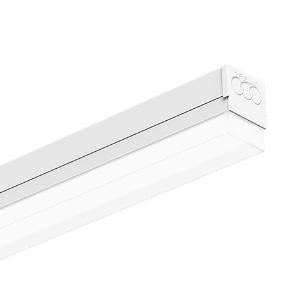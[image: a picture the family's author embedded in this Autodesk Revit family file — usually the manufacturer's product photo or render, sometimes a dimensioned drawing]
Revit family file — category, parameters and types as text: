
# Revit family: 3f_filippi_-_3f_zeta_dr_3f_filippi_-_10968_-_3f_zeta_dr_1x18_led_dali_l1194
name_source: partatom
category: Lighting Fixtures
units: mm (PartAtom-declared; Revit-internal decimal feet)

## family parameters
Cut with Voids When Loaded = No
Host = Face
Light Source = No
Part Type = Normal
Room Calculation Point = No
Round Connector Dimension = Use Diameter
Shared = No

## types (1)
- 3F Filippi - 3F Zeta DR (1 x LED, 2425 lm, 20 W, 4000 K)
    Apparent Load = 20 VA
    Approval mark = CE
    CIE Flux Codes = 41 72 91 86 100
    Color Rendering = 80
    Color Temperature = 4000 K
    Control Gear = Electronic transformer
    Default Elevation = 1800 mm
    Description = ILLUMINOTECHNICAL
Luminous efficiency 100% (DLOR 86%, ULOR 14%).
Initial luminous flux of the luminaire 2425 lm.
Diffused symmetric distribution.
Installation Interdistance Transv.D = 1.31 x hu - Long.D = 1.25 x hu.
Tabular UGR (CIE 117 - 4H-8H; S=0.25H; 70/50/20): RUG 23.1 - 21.7.
Beam angle: 136° - 112°.
Luminous efficacy 121 lm/W.
Lifetime (L93/B10): 30000 h. (tq+25°C)
Lifetime (L90/B10): 50000 h. (tq+25°C)
Lifetime (L85/B10): 80000 h. (tq+25°C)
Lifetime (L80/B10): 100000 h. (tq+25°C)
Sudden decreased luminous flux after 50000 hours: 0% (C0).
Photobiological safety in compliance with IEC/TR 62778: RG0 risk exempt, (IEC 62471).
In compliance with IEC/EN 62722-2-1 - IEC/EN 62717 standards.

SOURCE
Linear LED module 18W/840.
Energy efficiency class (UE 2019/2020 - UE 2019/2015): D.
CIE 13.3 Colour rendering index: CRI >80 (R9 <50%).
IES TM-30 Fidelity Index: Rf = 84 Rg = 95.
CCT nominal colour temperature 4000 K.
Colour initial tolerance (MacAdam): SDCM 3.

MECHANICAL
Housing in hot-galvanised steel, painted in white polyester, obtained through rolling process.
Light unit in hot-galvanised steel, painted in white polyester base with fixing springs and retractable safety hooks in stainless steel.
Rectangular screen in self-extinguishing polycarbonate, UV stabilised, opal, with smooth outer surface.
End caps in white polycarbonate.
Pair of stainless steel sliding brackets with sliding block screws.
Luminaire with limited surface temperature. - D - (EN 60598-2-24)
Dimensions: 1194x62 mm, height 81 mm. Weight 3.3 kg.
IP40 protection degree.
Mechanical strength to impacts IK06 (1 joule).
Glow-wire test resistance 850°C.

ELECTRICAL
Halogen Free DALI-2 DATI (Parts 251, 252, 253), PUSH-DIM, electronic wiring 230V-50/60Hz, power factor 0.90 at full load, THD <25%, constant output current, SELV, class I, 1 driver, 1 DALI addresse.
Power of the luminaire 20 W.
ENEC - CE.
SAFE FLICKER: PstLM=<1 and SVM=<0.4 (IEC TR 61547-1 and IEC TR 63158), to ensure a more comfortable and safe light.
Luminaire compliant with EN 60598-2-22 for power supply from a centralised emergency system CPSS (Central Power Supply System), not incorporated in the luminaire - high risk areas excluded. The default power and flux are 100% in AC and 15% in DC.
Ambient temperature from 0°C to +25°C.
Temperature class T6 max 85°C.
Relative humidity UR: <85%.

INSTALLATION
Ceiling / Suspended / Wall.
All accessories dedicated to this product are available on the Catalog and on our website www.3F-Filippi.com.

APPLICATIONS
Suitable product for food production plants (HACCP), IFS (Food Version 6), BRC (GSFS Food Version 7).
In commercial environments, exhibition areas, shops and stores.

LIGHT MANAGEMENT
Recommended minimum setting: 10%.
The luminaire, equipped with (DALI-2 DATI) driver, can be controlled manually with 3F Easy Dim technology or automatically/manually with wired or wireless DALI/D2D control systems.
The D2D driver guarantees interoperability with other devices with the same certification by making the following information available:
Device Data (Part 251), Energy Report (Part 252), Diagnosis & Maintenance (Part 253).
In electrical systems without a regulation system (manual or automatic) and DALI bus, a suitable jumper must be made on the DA-DA terminals of the appliance.

WARNING
Luminaire designed for disposal/recycling at end-of-life.
Replaceable (LED only) light source by a professional. Replaceable control gear by a professional.
    Height = 81 mm
    Lamp = 1 x LED
    Lamp Light Flux = 2425 lm
    Lamp Power = 20 W
    Lamp count = 1
    Length = 1194 mm
    Lifetime = 50000 h
    Luminous efficacy = 121 lm/W
    Manufacturer = 3F Filippi
    ModVariant = No
    Model = 3F Filippi - 10968 - 3F Zeta DR 1x18 LED DALI L1194
    Mounting Place = Ceiling
    Mounting Type = Pendant
    Number of Poles = 1
    OnlyDefault = Yes
    Power Factor = 1
    Product Name = 3F Filippi - 3F Zeta DR
    Product group = pendant luminaire
    ProductGroupID = 9
    Protection Class = Protection class I
    Protection Degree = IP 40
    RLX_Detail_Level = 1
    RLX_Emergency_Light_Flux = 0 lm
    RLX_Emergency_Type = 0
    RLX_Emergency_Type_DB = No
    RlxData = <blob elided: 35369 chars, md5=790831e2>
    Socket = socket
    Standby Power = 0 W
    System Light Flux = 2425 lm
    System Power = 20 W
    Type Comments = Product without accessories
    Type Image = 3ffilippi_3f_zeta_dr.jpg
    URL = http://relux.com
    VarID = ---
    Voltage = 0 V
    Weight = 0.00 kg
    Width = 62 mm  [stored 0.203412 ft]

note: [stored X ft] marks values corroborated as IEEE doubles in the binary element streams (Revit-internal decimal feet)

## geometry (parser evidence)
native form markers: Blend x4, Sweep x13
no freeform markers — native parametric forms only
